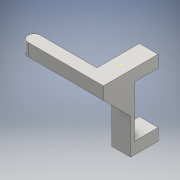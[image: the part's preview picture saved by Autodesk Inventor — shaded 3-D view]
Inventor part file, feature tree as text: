
AUTODESK INVENTOR PART (.ipt)
format: ipt  version: 2016 (Build 200138000, 138)  size: 138,240 bytes
history: native  units: mm
features: sketch x6, extrude x5, fillet x1
ambient origin geometry x8: Origin, YZ Plane, XZ Plane, XY Plane, X Axis, Y Axis, Z Axis, Center Point
bodies: Solid1 (feature_tree)
feature tree (12):
  extrude  "Extrusion1"  Depth=60.0mm
  extrude  "Extrusion2"  Depth=41.0mm
  extrude  "Extrusion3"  Depth=10.0mm
  extrude  "Extrusion5"  Depth=15.0mm TaperAngle=0.0deg
  extrude  "Extrusion6"  Depth=15.0mm TaperAngle=0.0deg
  sketch  "Sketch7"  dims[d19=50.0mm d20=0.0mm d21=5.0mm]
  fillet  "Fillet1"  Radius=9.871mm
  sketch  "Sketch1"  dims[d0=15.0mm d1=60.0mm]
  sketch  "Sketch2"  dims[d2=3.0mm d3=0.0mm d4=41.0mm]
  sketch  "Sketch3"  dims[d5=19.0mm d6=0.0mm d7=10.0mm]
  sketch  "Sketch5"  dims[d8=21.64mm d9=15.0mm d10=0.0mm]
  sketch  "Sketch6"  dims[d15=45.0deg d16=15.0mm d17=0.0mm d18=9.871mm]
